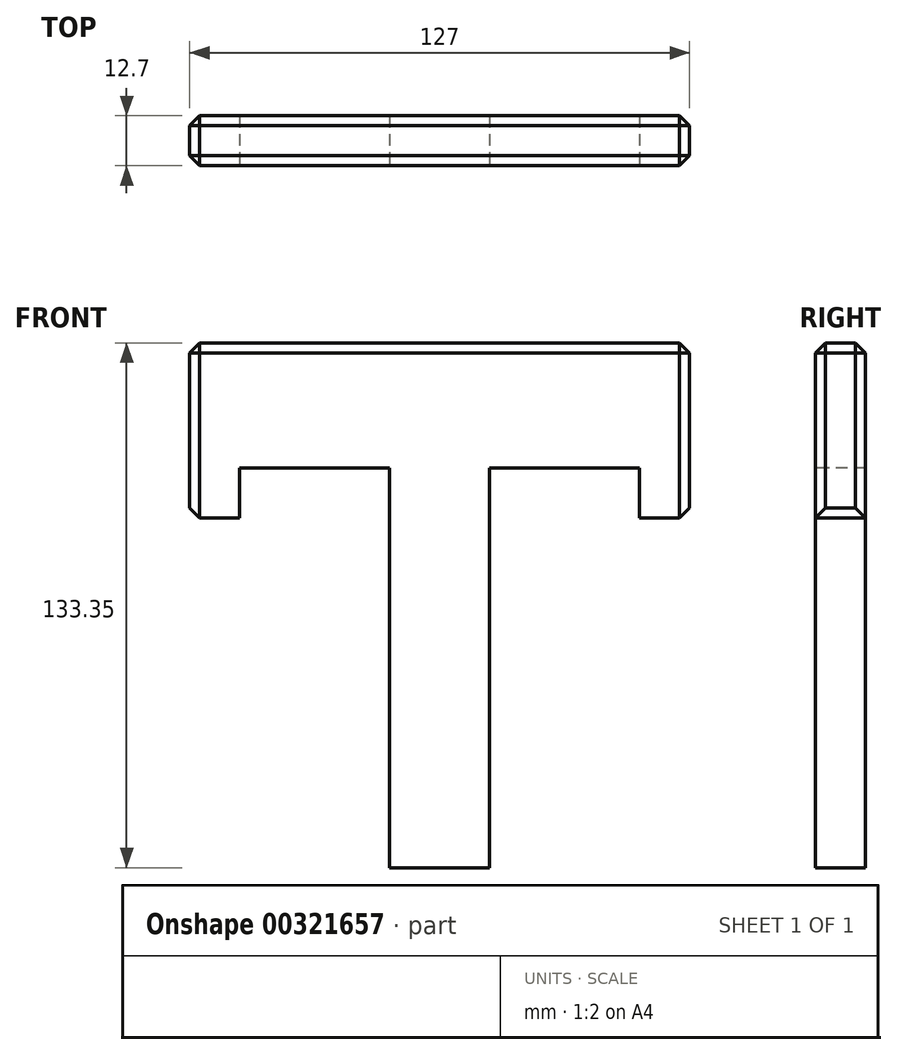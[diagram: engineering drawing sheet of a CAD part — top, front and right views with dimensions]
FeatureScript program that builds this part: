
annotation { "Feature Type Name" : "Feature", "Feature Type Description" : "" }
export const myFeature = defineFeature(function(context is Context, id is Id, definition is map)
    precondition{}
    {
        {
            var Q0;
            Q0=qCreatedBy(makeId("Front.planeOp"),FACE);
            var sketch = newSketch(context, id + "F0", { "sketchPlane" : qUnion([Q0])});
            skLineSegment(sketch, "E0", {"start": v(0.5, -61.23) * mm, "end": v(0.5, 40.37) * mm});
            skLineSegment(sketch, "E1", {"start": v(0.5, 40.37) * mm, "end": v(38.6, 40.37) * mm});
            skLineSegment(sketch, "E2", {"start": v(38.6, 40.37) * mm, "end": v(38.6, 27.67) * mm});
            skLineSegment(sketch, "E3", {"start": v(38.6, 27.67) * mm, "end": v(51.3, 27.67) * mm});
            skLineSegment(sketch, "E4", {"start": v(51.3, 27.67) * mm, "end": v(51.3, 72.12) * mm});
            skLineSegment(sketch, "E5", {"start": v(51.3, 72.12) * mm, "end": v(-75.7, 72.12) * mm});
            skLineSegment(sketch, "E6", {"start": v(-75.7, 72.12) * mm, "end": v(-75.7, 27.67) * mm});
            skLineSegment(sketch, "E7", {"start": v(-75.7, 27.67) * mm, "end": v(-63, 27.67) * mm});
            skLineSegment(sketch, "E8", {"start": v(-63, 27.67) * mm, "end": v(-63, 40.37) * mm});
            skLineSegment(sketch, "E9", {"start": v(-63, 40.37) * mm, "end": v(-24.9, 40.37) * mm});
            skLineSegment(sketch, "E10", {"start": v(-24.9, 40.37) * mm, "end": v(-24.9, -61.23) * mm});
            skLineSegment(sketch, "E11", {"start": v(-24.9, -61.23) * mm, "end": v(0.5, -61.23) * mm});
            skSolve(sketch);
        }
        {
            var Q0;
            Q0=makeQuery(id+"F0.imprint","IMPRINT",FACE,{"disambiguationData":[TD([[makeQuery(id+"F0.imprint","IMPRINT",EDGE,{"derivedFrom":sQuery(id+"F0.wireOp",EDGE,"E0")}),1.0]])]});
            extrude(context, id + "F1", {"entities" : qUnion([Q0]), "oppositeDirection" : true, "depth" : 12.7 * mm});
        }
        {
            var Q0;
            Q0=makeQuery(id+"F1.opExtrude","CAP_EDGE",EDGE,{"disambiguationData":[OSD([sQuery(id+"F0.wireOp",EDGE,"E5")])],"isStart":true});
            var Q1;
            Q1=makeQuery(id+"F1.opExtrude","SWEPT_EDGE",EDGE,{"disambiguationData":[OSD([sQuery(id+"F0.wireOp",EDGE,"E4"),sQuery(id+"F0.wireOp",EDGE,"E5")])]});
            var Q2;
            Q2=makeQuery(id+"F1.opExtrude","CAP_EDGE",EDGE,{"disambiguationData":[OSD([sQuery(id+"F0.wireOp",EDGE,"E5")])],"isStart":false});
            var Q3;
            Q3=makeQuery(id+"F1.opExtrude","SWEPT_EDGE",EDGE,{"disambiguationData":[OSD([sQuery(id+"F0.wireOp",EDGE,"E5"),sQuery(id+"F0.wireOp",EDGE,"E6")])]});
            var Q4;
            Q4=makeQuery(id+"F1.opExtrude","SWEPT_EDGE",EDGE,{"disambiguationData":[OSD([sQuery(id+"F0.wireOp",EDGE,"E3"),sQuery(id+"F0.wireOp",EDGE,"E4")])]});
            var Q5;
            Q5=makeQuery(id+"F1.opExtrude","CAP_EDGE",EDGE,{"disambiguationData":[OSD([sQuery(id+"F0.wireOp",EDGE,"E4")])],"isStart":true});
            var Q6;
            Q6=makeQuery(id+"F1.opExtrude","SWEPT_FACE",FACE,{"disambiguationData":[OSD([sQuery(id+"F0.wireOp",EDGE,"E4")])]});
            var Q7;
            Q7=makeQuery(id+"F1.opExtrude","SWEPT_FACE",FACE,{"disambiguationData":[OSD([sQuery(id+"F0.wireOp",EDGE,"E6")])]});
            chamfer(context, id + "F2", {"entities" : qUnion([Q0, Q1, Q2, Q3, Q4, Q5, Q6, Q7]), "width" : 2.54 * mm, "tangentPropagation" : true});
        }
    });
